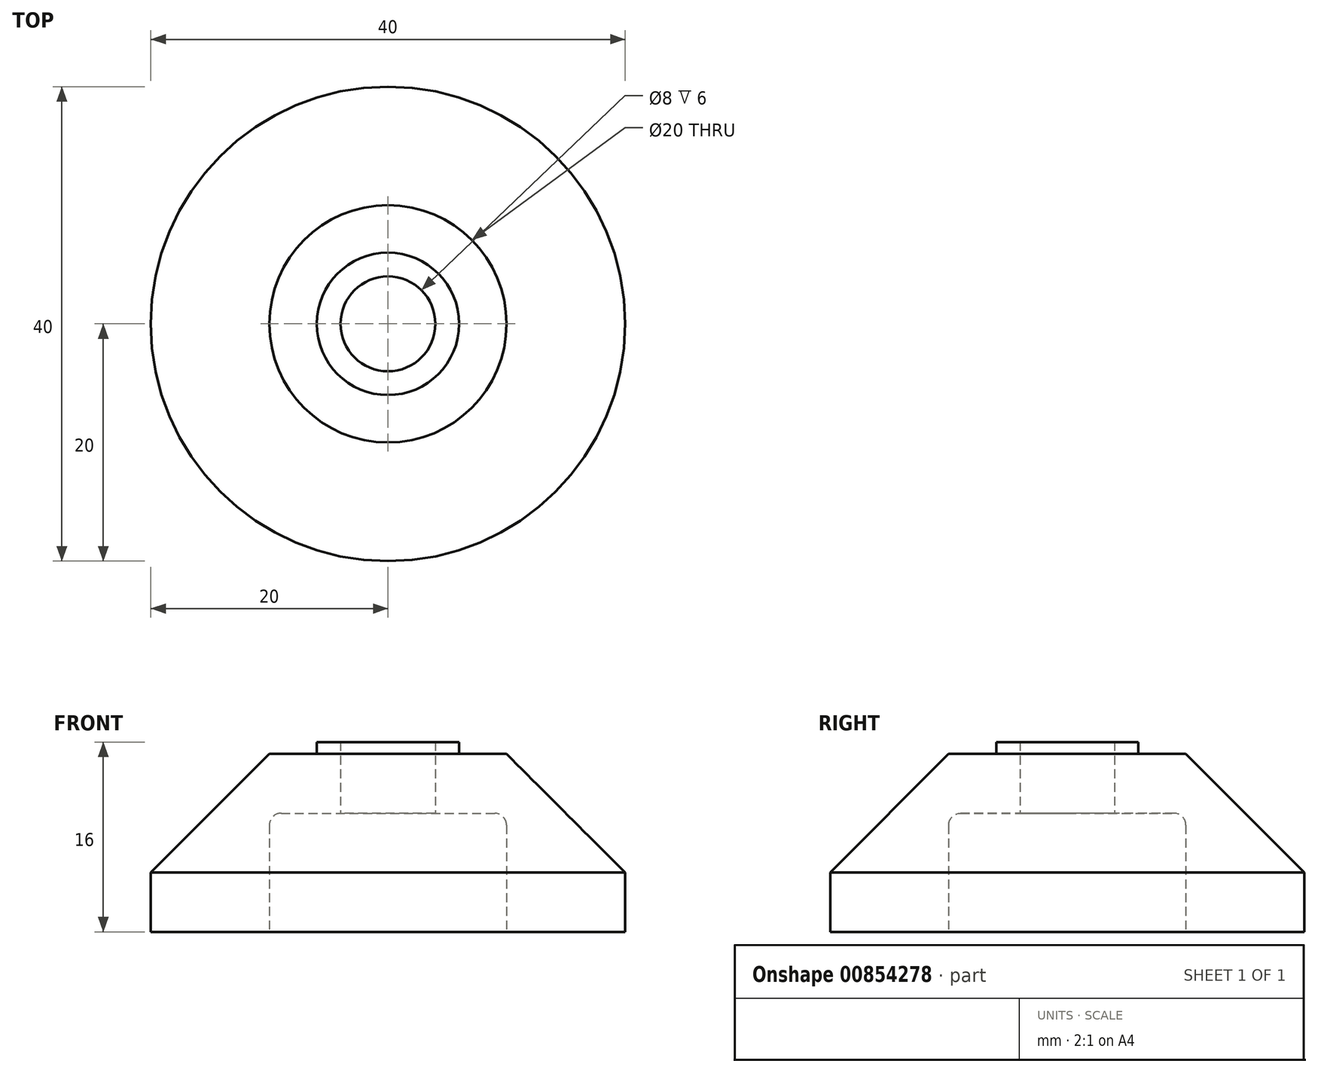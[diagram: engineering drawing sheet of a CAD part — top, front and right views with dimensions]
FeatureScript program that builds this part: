
annotation { "Feature Type Name" : "Feature", "Feature Type Description" : "" }
export const myFeature = defineFeature(function(context is Context, id is Id, definition is map)
    precondition{}
    {
        {
            var Q0;
            Q0=qCreatedBy(makeId("Top.planeOp"),FACE);
            var sketch = newSketch(context, id + "F0", { "sketchPlane" : qUnion([Q0])});
            skCircle(sketch, "E0", {"center": v(0, 0) * mm, "radius": 20 * mm});
            skSolve(sketch);
        }
        {
            var Q0;
            Q0=makeQuery(id+"F0.imprint","IMPRINT",FACE,{"disambiguationData":[TD([[makeQuery(id+"F0.imprint","IMPRINT",EDGE,{"derivedFrom":sQuery(id+"F0.wireOp",EDGE,"E0")}),1.0]])]});
            extrude(context, id + "F1", {"entities" : qUnion([Q0]), "depth" : 15 * mm, "offsetDistance" : 25 * mm});
        }
        {
            var Q0;
            Q0=makeQuery(id+"F1.opExtrude","CAP_EDGE",EDGE,{"disambiguationData":[OSD([sQuery(id+"F0.wireOp",EDGE,"E0")])],"isStart":false});
            chamfer(context, id + "F2", {"entities" : qUnion([Q0]), "width" : 10 * mm, "tangentPropagation" : true});
        }
        {
            var Q0;
            Q0=makeQuery(id+"F1.opExtrude","CAP_FACE",FACE,{"disambiguationData":[OSD([sQuery(id+"F0.wireOp",EDGE,"E0")])],"isStart":false});
            var sketch = newSketch(context, id + "F3", { "sketchPlane" : qUnion([Q0])});
            skCircle(sketch, "E1.0.0", {"center": v(0, 0) * mm, "radius": 10 * mm});
            skCircle(sketch, "E2", {"center": v(0, 0) * mm, "radius": 6 * mm});
            skCircle(sketch, "E3", {"center": v(0, 0) * mm, "radius": 4 * mm});
            skSolve(sketch);
        }
        {
            var Q0;
            Q0=makeQuery(id+"F3.imprint","IMPRINT",FACE,{"disambiguationData":[TD([[makeQuery(id+"F3.imprint","IMPRINT",EDGE,{"derivedFrom":sQuery(id+"F3.wireOp",EDGE,"E2")}),1.0]])]});
            extrude(context, id + "F4", {"entities" : qUnion([Q0]), "operationType" : NewBodyOperationType.ADD, "depth" : 1 * mm, "offsetDistance" : 25 * mm});
        }
        {
            var Q0;
            Q0=makeQuery(id+"F4.boolean.opBoolean","SPLIT",FACE,{"disambiguationData":[TD([makeQuery(id+"F4.opExtrude","SWEPT_FACE",FACE,{"disambiguationData":[OSD([sQuery(id+"F3.wireOp",EDGE,"E3")])]})])],"derivedFrom":makeQuery(id+"F1.opExtrude","CAP_FACE",FACE,{"disambiguationData":[OSD([sQuery(id+"F0.wireOp",EDGE,"E0")])],"isStart":false})});
            var sketch = newSketch(context, id + "F5", { "sketchPlane" : qUnion([Q0])});
            skCircle(sketch, "E4.0.0", {"center": v(0, 0) * mm, "radius": 4 * mm});
            skSolve(sketch);
        }
        {
            var Q0;
            Q0=makeQuery(id+"F5.imprint","IMPRINT",FACE,{"disambiguationData":[TD([[makeQuery(id+"F5.imprint","IMPRINT",EDGE,{"derivedFrom":sQuery(id+"F5.wireOp",EDGE,"E4.0.0")}),1.0]])]});
            extrude(context, id + "F6", {"entities" : qUnion([Q0]), "operationType" : NewBodyOperationType.REMOVE, "endBound" : BoundingType.THROUGH_ALL, "oppositeDirection" : true, "depth" : 25 * mm, "offsetDistance" : 25 * mm});
        }
        {
            var Q0;
            Q0=makeQuery(id+"F1.opExtrude","CAP_FACE",FACE,{"disambiguationData":[OSD([sQuery(id+"F0.wireOp",EDGE,"E0")])],"isStart":true});
            var sketch = newSketch(context, id + "F7", { "sketchPlane" : qUnion([Q0])});
            skCircle(sketch, "E5.0.0", {"center": v(0, 0) * mm, "radius": 20 * mm});
            skCircle(sketch, "E6", {"center": v(0, 0) * mm, "radius": 10 * mm});
            skSolve(sketch);
        }
        {
            var Q0;
            Q0=makeQuery(id+"F7.imprint","IMPRINT",FACE,{"disambiguationData":[TD([[makeQuery(id+"F7.imprint","IMPRINT",EDGE,{"derivedFrom":sQuery(id+"F7.wireOp",EDGE,"E6")}),1.0]])]});
            extrude(context, id + "F8", {"entities" : qUnion([Q0]), "operationType" : NewBodyOperationType.REMOVE, "oppositeDirection" : true, "depth" : 10 * mm, "offsetDistance" : 25 * mm});
        }
        {
            var Q0;
            Q0=makeQuery(id+"F8.boolean.opBoolean","COPY",EDGE,{"derivedFrom":makeQuery(id+"F8.opExtrude","CAP_EDGE",EDGE,{"disambiguationData":[OSD([sQuery(id+"F7.wireOp",EDGE,"E6")])],"isStart":false})});
            fillet(context, id + "F9", {"entities" : qUnion([Q0]), "radius" : 1 * mm, "tangentPropagation" : true, "allowEdgeOverflow" : false});
        }
    });
